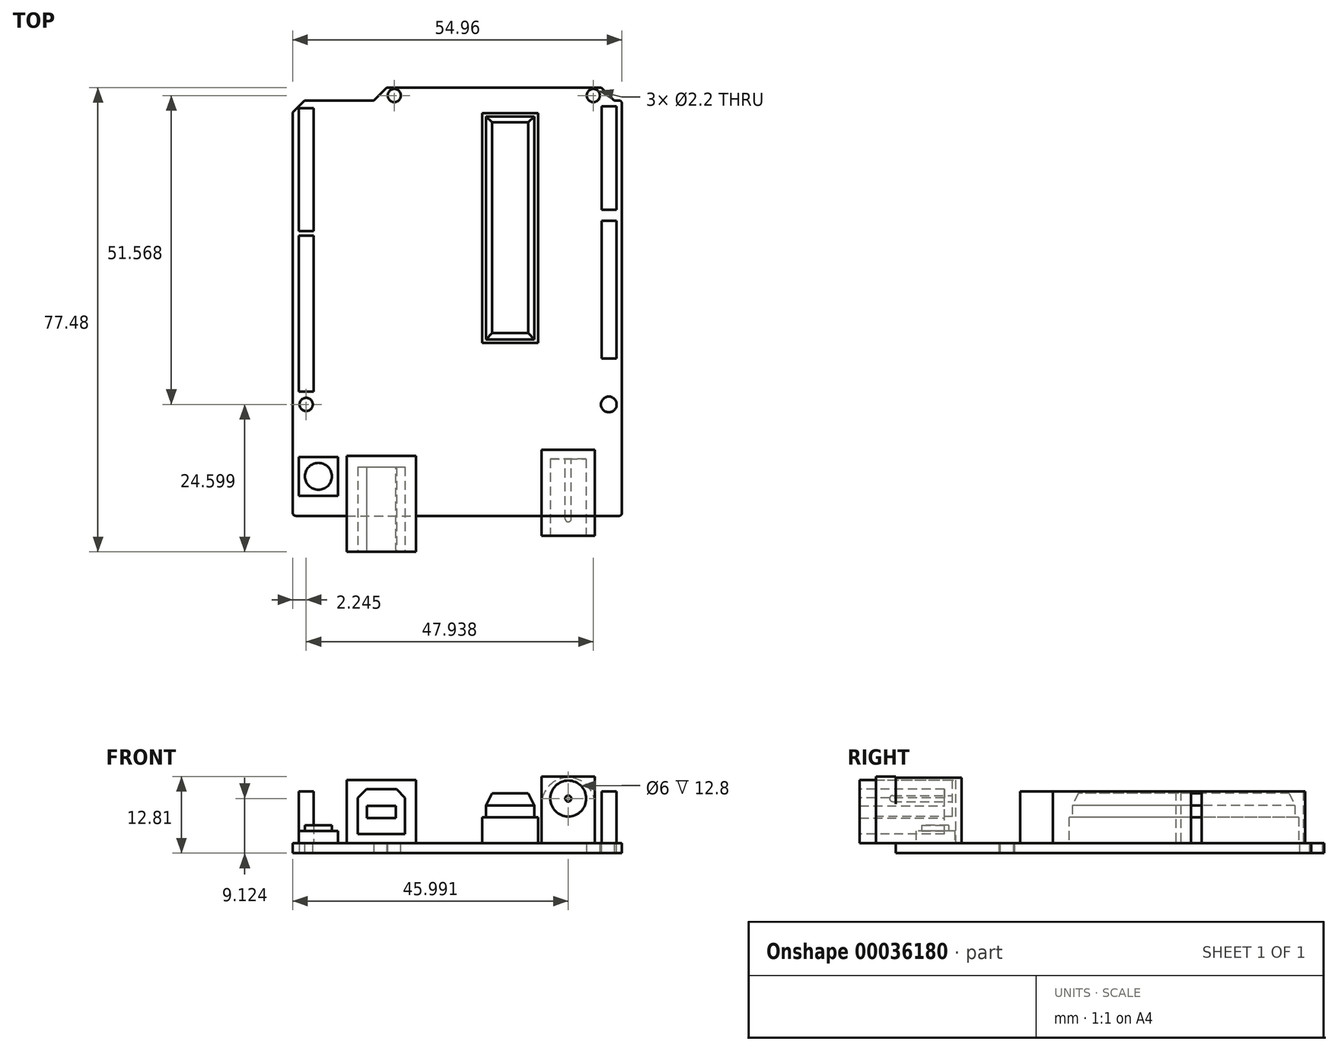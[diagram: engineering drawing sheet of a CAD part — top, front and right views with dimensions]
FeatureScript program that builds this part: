
annotation { "Feature Type Name" : "Feature", "Feature Type Description" : "" }
export const myFeature = defineFeature(function(context is Context, id is Id, definition is map)
    precondition{}
    {
        {
            var Q0;
            Q0=qCreatedBy(makeId("Top.planeOp"),FACE);
            var sketch = newSketch(context, id + "F0", { "sketchPlane" : qUnion([Q0])});
            skLineSegment(sketch, "E0.rect.bottom", {"start": v(-11.81, 35.74) * mm, "end": v(24.03, 35.74) * mm});
            skLineSegment(sketch, "E0.rect.top", {"start": v(-26.94, -35.74) * mm, "end": v(26.97, -35.74) * mm});
            skLineSegment(sketch, "E0.rect.left", {"start": v(-27.48, 31.62) * mm, "end": v(-27.48, -35.2) * mm});
            skLineSegment(sketch, "E0.rect.right", {"start": v(27.48, 33.07) * mm, "end": v(27.48, -35.23) * mm});
            skPoint(sketch, "E0.rect.middle", {"position": v(0, 0) * mm});
            skLineSegment(sketch, "E1.top", {"start": v(-25.49, 33.6) * mm, "end": v(-13.95, 33.6) * mm});
            skPoint(sketch, "E2.orphan", {"position": v(-27.48, 35.74) * mm});
            skLineSegment(sketch, "E3", {"start": v(-27.48, 31.62) * mm, "end": v(-25.49, 33.6) * mm});
            skLineSegment(sketch, "E4", {"start": v(-11.81, 35.74) * mm, "end": v(-13.95, 33.6) * mm});
            skLineSegment(sketch, "E5.top", {"start": v(26.17, 33.6) * mm, "end": v(26.94, 33.6) * mm});
            skLineSegment(sketch, "E6", {"start": v(24.03, 35.74) * mm, "end": v(26.17, 33.6) * mm});
            skPoint(sketch, "E7.orphan", {"position": v(27.48, 35.74) * mm});
            skPoint(sketch, "E8.visualSharp", {"position": v(27.48, -35.74) * mm});
            skArc(sketch, "E8.filletArc", {"start": v(26.97, -35.74) * mm, "mid": v(27.33, -35.6) * mm, "end": v(27.48, -35.23) * mm});
            skPoint(sketch, "E9.visualSharp", {"position": v(27.48, 33.6) * mm});
            skArc(sketch, "E9.filletArc", {"start": v(27.48, 33.07) * mm, "mid": v(27.32, 33.45) * mm, "end": v(26.94, 33.6) * mm});
            skPoint(sketch, "E10.visualSharp", {"position": v(-27.48, -35.74) * mm});
            skArc(sketch, "E10.filletArc", {"start": v(-27.48, -35.2) * mm, "mid": v(-27.32, -35.59) * mm, "end": v(-26.94, -35.74) * mm});
            skPoint(sketch, "E11.second.point", {"position": v(21.12, -10.57) * mm});
            skPoint(sketch, "E11.third.point", {"position": v(22.07, -8.93) * mm});
            skLineSegment(sketch, "E12", {"start": v(-13.95, 33.6) * mm, "end": v(31.22, 33.6) * mm, "construction": true});
            skSolve(sketch);
        }
        {
            var Q0;
            Q0=makeQuery(id+"F0.imprint","IMPRINT",FACE,{"disambiguationData":[TD([[makeQuery(id+"F0.imprint","IMPRINT",EDGE,{"derivedFrom":sQuery(id+"F0.wireOp",EDGE,"E0.rect.bottom")}),-1.0]])]});
            extrude(context, id + "F1", {"entities" : qUnion([Q0]), "depth" : 1.69 * mm});
        }
        {
            var Q0;
            Q0=makeQuery(id+"F1.opExtrude","CAP_FACE",FACE,{"disambiguationData":[OSD([sQuery(id+"F0.wireOp",EDGE,"E0.rect.bottom"),sQuery(id+"F0.wireOp",EDGE,"E0.rect.top"),sQuery(id+"F0.wireOp",EDGE,"E0.rect.left"),sQuery(id+"F0.wireOp",EDGE,"E0.rect.right"),sQuery(id+"F0.wireOp",EDGE,"E1.top"),sQuery(id+"F0.wireOp",EDGE,"E3"),sQuery(id+"F0.wireOp",EDGE,"E4"),sQuery(id+"F0.wireOp",EDGE,"E5.top"),sQuery(id+"F0.wireOp",EDGE,"E6"),sQuery(id+"F0.wireOp",EDGE,"E8.filletArc"),sQuery(id+"F0.wireOp",EDGE,"E9.filletArc"),sQuery(id+"F0.wireOp",EDGE,"E10.filletArc")])],"isStart":false});
            var sketch = newSketch(context, id + "F2", { "sketchPlane" : qUnion([Q0])});
            skLineSegment(sketch, "E13.top", {"start": v(24.1, -9.48) * mm, "end": v(26.53, -9.48) * mm});
            skLineSegment(sketch, "E13.left", {"start": v(24.1, 32.6) * mm, "end": v(24.1, 15.32) * mm});
            skLineSegment(sketch, "E13.right", {"start": v(26.53, 32.6) * mm, "end": v(26.53, 15.32) * mm});
            skLineSegment(sketch, "E14", {"start": v(24.1, 32.6) * mm, "end": v(26.53, 32.6) * mm});
            skLineSegment(sketch, "E15", {"start": v(24.1, 15.32) * mm, "end": v(26.53, 15.32) * mm});
            skLineSegment(sketch, "E16", {"start": v(24.1, 13.52) * mm, "end": v(26.53, 13.52) * mm});
            skLineSegment(sketch, "E17.trimOffspring", {"start": v(24.1, 13.52) * mm, "end": v(24.1, -9.48) * mm});
            skLineSegment(sketch, "E18.trimOffspring", {"start": v(26.53, 13.52) * mm, "end": v(26.53, -9.48) * mm});
            skLineSegment(sketch, "E19.bottom", {"start": v(-26.48, 32.3) * mm, "end": v(-23.98, 32.3) * mm});
            skLineSegment(sketch, "E19.top", {"start": v(-26.48, -14.99) * mm, "end": v(-23.98, -14.99) * mm});
            skLineSegment(sketch, "E19.left", {"start": v(-26.48, 32.3) * mm, "end": v(-26.48, 11.81) * mm});
            skLineSegment(sketch, "E19.right", {"start": v(-23.98, 32.3) * mm, "end": v(-23.98, 11.81) * mm});
            skLineSegment(sketch, "E20.bottom", {"start": v(-26.48, 11.81) * mm, "end": v(-23.98, 11.81) * mm});
            skLineSegment(sketch, "E20.top", {"start": v(-26.48, 11.01) * mm, "end": v(-23.98, 11.01) * mm});
            skLineSegment(sketch, "E21.trimOffspring", {"start": v(-23.98, 11.01) * mm, "end": v(-23.98, -14.99) * mm});
            skLineSegment(sketch, "E22.trimOffspring", {"start": v(-26.48, 11.01) * mm, "end": v(-26.48, -14.99) * mm});
            skSolve(sketch);
        }
        {
            var Q0;
            Q0=makeQuery(id+"F2.imprint","IMPRINT",FACE,{"disambiguationData":[TD([[makeQuery(id+"F2.imprint","IMPRINT",EDGE,{"derivedFrom":sQuery(id+"F2.wireOp",EDGE,"E13.top")}),1.0]])]});
            var Q1;
            Q1=makeQuery(id+"F2.imprint","IMPRINT",FACE,{"disambiguationData":[TD([[makeQuery(id+"F2.imprint","IMPRINT",EDGE,{"derivedFrom":sQuery(id+"F2.wireOp",EDGE,"E13.left")}),1.0]])]});
            var Q2;
            Q2=makeQuery(id+"F2.imprint","IMPRINT",FACE,{"disambiguationData":[TD([[makeQuery(id+"F2.imprint","IMPRINT",EDGE,{"derivedFrom":sQuery(id+"F2.wireOp",EDGE,"E19.bottom")}),-1.0]])]});
            var Q3;
            Q3=makeQuery(id+"F2.imprint","IMPRINT",FACE,{"disambiguationData":[TD([[makeQuery(id+"F2.imprint","IMPRINT",EDGE,{"derivedFrom":sQuery(id+"F2.wireOp",EDGE,"E19.top")}),1.0]])]});
            extrude(context, id + "F3", {"entities" : qUnion([Q0, Q1, Q2, Q3]), "depth" : 8.6 * mm});
        }
        {
            var Q0;
            Q0=makeQuery(id+"F1.opExtrude","SWEPT_FACE",FACE,{"disambiguationData":[OSD([sQuery(id+"F0.wireOp",EDGE,"E0.rect.top")])]});
            cPlane(context, id + "F4", {"entities" : qUnion([Q0]), "cplaneType" : CPlaneType.OFFSET, "offset" : 0 * mm, "width" : 150 * mm, "height" : 150 * mm});
        }
        {
            var Q0;
            Q0=qCreatedBy(id+"F4.planeOp",FACE);
            var sketch = newSketch(context, id + "F5", { "sketchPlane" : qUnion([Q0])});
            skLineSegment(sketch, "E23", {"start": v(30.92, 1.68) * mm, "end": v(22.95, 1.68) * mm, "construction": true});
            skLineSegment(sketch, "E24.bottom", {"start": v(22.95, 1.68) * mm, "end": v(14.07, 1.68) * mm});
            skLineSegment(sketch, "E24.left", {"start": v(22.95, 1.68) * mm, "end": v(22.95, 8.18) * mm});
            skLineSegment(sketch, "E24.right", {"start": v(14.07, 1.68) * mm, "end": v(14.07, 8.18) * mm});
            skArc(sketch, "E25", {"start": v(22.95, 8.18) * mm, "mid": v(18.51, 12.62) * mm, "end": v(14.07, 8.18) * mm});
            skSolve(sketch);
        }
        {
            var Q0;
            Q0=makeQuery(id+"F5.imprint","IMPRINT",FACE,{"disambiguationData":[TD([[makeQuery(id+"F5.imprint","IMPRINT",EDGE,{"derivedFrom":sQuery(id+"F5.wireOp",EDGE,"E24.bottom")}),-1.0]])]});
            extrude(context, id + "F6", {"entities" : qUnion([Q0]), "oppositeDirection" : true, "depth" : 11 * mm});
        }
        {
            var Q0;
            Q0=qCreatedBy(id+"F4.planeOp",FACE);
            var sketch = newSketch(context, id + "F7", { "sketchPlane" : qUnion([Q0])});
            skLineSegment(sketch, "E26.bottom", {"start": v(14.07, 1.69) * mm, "end": v(22.95, 1.69) * mm});
            skLineSegment(sketch, "E26.top", {"start": v(14.07, 12.81) * mm, "end": v(22.95, 12.81) * mm});
            skLineSegment(sketch, "E26.left", {"start": v(14.07, 1.69) * mm, "end": v(14.07, 12.81) * mm});
            skLineSegment(sketch, "E26.right", {"start": v(22.95, 1.69) * mm, "end": v(22.95, 12.81) * mm});
            skSolve(sketch);
        }
        {
            var Q0;
            Q0=makeQuery(id+"F7.imprint","IMPRINT",FACE,{"disambiguationData":[TD([[makeQuery(id+"F7.imprint","IMPRINT",EDGE,{"derivedFrom":sQuery(id+"F7.wireOp",EDGE,"E26.bottom")}),1.0]])]});
            extrude(context, id + "F8", {"entities" : qUnion([Q0]), "operationType" : NewBodyOperationType.ADD, "depth" : 3.3 * mm});
        }
        {
            var Q0;
            Q0=makeQuery(id+"F8.opExtrude","CAP_FACE",FACE,{"disambiguationData":[OSD([sQuery(id+"F7.wireOp",EDGE,"E26.bottom"),sQuery(id+"F7.wireOp",EDGE,"E26.top"),sQuery(id+"F7.wireOp",EDGE,"E26.left"),sQuery(id+"F7.wireOp",EDGE,"E26.right")])],"isStart":false});
            var sketch = newSketch(context, id + "F9", { "sketchPlane" : qUnion([Q0])});
            skCircle(sketch, "E27", {"center": v(18.51, 9.12) * mm, "radius": 3 * mm});
            skSolve(sketch);
        }
        {
            var Q0;
            Q0=makeQuery(id+"F9.imprint","IMPRINT",FACE,{"disambiguationData":[TD([[makeQuery(id+"F9.imprint","IMPRINT",EDGE,{"derivedFrom":sQuery(id+"F9.wireOp",EDGE,"E27")}),1.0]])]});
            var Q1;
            Q1=sQuery(id+"F9.wireOp",EDGE,"E27");
            extrude(context, id + "F10", {"entities" : qUnion([Q0]), "operationType" : NewBodyOperationType.REMOVE, "surfaceEntities" : qUnion([Q1]), "oppositeDirection" : true, "depth" : 12.8 * mm});
        }
        {
            var Q0;
            Q0=makeQuery(id+"F10.boolean.opBoolean","COPY",FACE,{"derivedFrom":makeQuery(id+"F10.opExtrude","CAP_FACE",FACE,{"disambiguationData":[OSD([sQuery(id+"F9.wireOp",EDGE,"E27")])],"isStart":false})});
            var sketch = newSketch(context, id + "F11", { "sketchPlane" : qUnion([Q0])});
            skCircle(sketch, "E28.0", {"center": v(18.51, 9.12) * mm, "radius": 3 * mm});
            skCircle(sketch, "E29", {"center": v(18.51, 9.12) * mm, "radius": 0.5 * mm});
            skSolve(sketch);
        }
        {
            var Q0;
            Q0=makeQuery(id+"F11.imprint","IMPRINT",FACE,{"disambiguationData":[TD([[makeQuery(id+"F11.imprint","IMPRINT",EDGE,{"derivedFrom":sQuery(id+"F11.wireOp",EDGE,"E29")}),1.0]])]});
            var Q1;
            Q1=sQuery(id+"F11.wireOp",EDGE,"E29");
            extrude(context, id + "F12", {"entities" : qUnion([Q0]), "surfaceEntities" : qUnion([Q1]), "depth" : 10 * mm});
        }
        {
            var Q0;
            Q0=makeQuery(id+"F1.opExtrude","CAP_FACE",FACE,{"disambiguationData":[OSD([sQuery(id+"F0.wireOp",EDGE,"E0.rect.bottom"),sQuery(id+"F0.wireOp",EDGE,"E0.rect.top"),sQuery(id+"F0.wireOp",EDGE,"E0.rect.left"),sQuery(id+"F0.wireOp",EDGE,"E0.rect.right"),sQuery(id+"F0.wireOp",EDGE,"E1.top"),sQuery(id+"F0.wireOp",EDGE,"E3"),sQuery(id+"F0.wireOp",EDGE,"E4"),sQuery(id+"F0.wireOp",EDGE,"E5.top"),sQuery(id+"F0.wireOp",EDGE,"E6"),sQuery(id+"F0.wireOp",EDGE,"E8.filletArc"),sQuery(id+"F0.wireOp",EDGE,"E9.filletArc"),sQuery(id+"F0.wireOp",EDGE,"E10.filletArc")])],"isStart":false});
            var sketch = newSketch(context, id + "F13", { "sketchPlane" : qUnion([Q0])});
            skLineSegment(sketch, "E30.bottom", {"start": v(-18.48, -35.74) * mm, "end": v(-6.88, -35.74) * mm});
            skLineSegment(sketch, "E30.top", {"start": v(-18.48, -25.74) * mm, "end": v(-6.88, -25.74) * mm});
            skLineSegment(sketch, "E30.left", {"start": v(-18.48, -35.74) * mm, "end": v(-18.48, -25.74) * mm});
            skLineSegment(sketch, "E30.right", {"start": v(-6.88, -35.74) * mm, "end": v(-6.88, -25.74) * mm});
            skSolve(sketch);
        }
        {
            var Q0;
            Q0=makeQuery(id+"F13.imprint","IMPRINT",FACE,{"disambiguationData":[TD([[makeQuery(id+"F13.imprint","IMPRINT",EDGE,{"derivedFrom":sQuery(id+"F13.wireOp",EDGE,"E30.bottom")}),1.0]])]});
            extrude(context, id + "F14", {"entities" : qUnion([Q0]), "depth" : 10.5 * mm});
        }
        {
            var Q0;
            Q0=makeQuery(id+"F14.opExtrude","SWEPT_FACE",FACE,{"disambiguationData":[OSD([sQuery(id+"F13.wireOp",EDGE,"E30.bottom")])]});
            var sketch = newSketch(context, id + "F15", { "sketchPlane" : qUnion([Q0])});
            skLineSegment(sketch, "E31.bottom", {"start": v(-18.48, 12.2) * mm, "end": v(-6.88, 12.2) * mm});
            skLineSegment(sketch, "E31.top", {"start": v(-18.48, 1.69) * mm, "end": v(-6.88, 1.69) * mm});
            skLineSegment(sketch, "E31.left", {"start": v(-18.48, 12.2) * mm, "end": v(-18.48, 1.69) * mm});
            skLineSegment(sketch, "E31.right", {"start": v(-6.88, 12.2) * mm, "end": v(-6.88, 1.69) * mm});
            skSolve(sketch);
        }
        {
            var Q0;
            Q0=makeQuery(id+"F15.imprint","IMPRINT",FACE,{"disambiguationData":[TD([[makeQuery(id+"F15.imprint","IMPRINT",EDGE,{"derivedFrom":sQuery(id+"F15.wireOp",EDGE,"E31.bottom")}),-1.0]])]});
            extrude(context, id + "F16", {"entities" : qUnion([Q0]), "operationType" : NewBodyOperationType.ADD, "depth" : 6 * mm});
        }
        {
            var Q0;
            Q0=makeQuery(id+"F16.opExtrude","CAP_FACE",FACE,{"disambiguationData":[OSD([sQuery(id+"F15.wireOp",EDGE,"E31.bottom"),sQuery(id+"F15.wireOp",EDGE,"E31.top"),sQuery(id+"F15.wireOp",EDGE,"E31.left"),sQuery(id+"F15.wireOp",EDGE,"E31.right")])],"isStart":false});
            var sketch = newSketch(context, id + "F17", { "sketchPlane" : qUnion([Q0])});
            skLineSegment(sketch, "E32.rect.bottom", {"start": v(-16.63, 3.2) * mm, "end": v(-8.73, 3.2) * mm});
            skLineSegment(sketch, "E32.rect.top", {"start": v(-15.19, 10.7) * mm, "end": v(-10.17, 10.7) * mm});
            skLineSegment(sketch, "E32.rect.left", {"start": v(-16.63, 3.2) * mm, "end": v(-16.63, 9.25) * mm});
            skLineSegment(sketch, "E32.rect.right", {"start": v(-8.73, 3.2) * mm, "end": v(-8.73, 9.25) * mm});
            skPoint(sketch, "E32.rect.middle", {"position": v(-12.68, 6.94) * mm});
            skPoint(sketch, "E32.rect.middle.positionSnap0", {"position": v(-18.48, 6.94) * mm});
            skPoint(sketch, "E32.rect.middle.positionSnap1", {"position": v(-12.68, 12.2) * mm});
            skPoint(sketch, "E32.rect.centerSnap0", {"position": v(-18.48, 6.94) * mm});
            skPoint(sketch, "E32.rect.centerSnap1", {"position": v(-12.68, 12.2) * mm});
            skLineSegment(sketch, "E33", {"start": v(-16.63, 9.25) * mm, "end": v(-15.19, 10.7) * mm});
            skLineSegment(sketch, "E34", {"start": v(-10.17, 10.7) * mm, "end": v(-8.73, 9.25) * mm});
            skPoint(sketch, "E35.orphan", {"position": v(-16.63, 10.7) * mm});
            skPoint(sketch, "E36.orphan", {"position": v(-8.73, 10.7) * mm});
            skSolve(sketch);
        }
        {
            var Q0;
            Q0=makeQuery(id+"F17.imprint","IMPRINT",FACE,{"disambiguationData":[TD([[makeQuery(id+"F17.imprint","IMPRINT",EDGE,{"derivedFrom":sQuery(id+"F17.wireOp",EDGE,"E32.rect.bottom")}),1.0]])]});
            extrude(context, id + "F18", {"entities" : qUnion([Q0]), "operationType" : NewBodyOperationType.REMOVE, "oppositeDirection" : true, "depth" : 14.14 * mm});
        }
        {
            var Q0;
            Q0=makeQuery(id+"F18.boolean.opBoolean","COPY",FACE,{"derivedFrom":makeQuery(id+"F18.opExtrude","CAP_FACE",FACE,{"disambiguationData":[OSD([sQuery(id+"F17.wireOp",EDGE,"E32.rect.bottom"),sQuery(id+"F17.wireOp",EDGE,"E32.rect.top"),sQuery(id+"F17.wireOp",EDGE,"E32.rect.left"),sQuery(id+"F17.wireOp",EDGE,"E32.rect.right"),sQuery(id+"F17.wireOp",EDGE,"E33"),sQuery(id+"F17.wireOp",EDGE,"E34")])],"isStart":false})});
            var sketch = newSketch(context, id + "F19", { "sketchPlane" : qUnion([Q0])});
            skLineSegment(sketch, "E37.rect.bottom", {"start": v(-15.12, 5.84) * mm, "end": v(-10.24, 5.84) * mm});
            skLineSegment(sketch, "E37.rect.top", {"start": v(-15.12, 7.92) * mm, "end": v(-10.24, 7.92) * mm});
            skLineSegment(sketch, "E37.rect.left", {"start": v(-15.12, 5.84) * mm, "end": v(-15.12, 7.92) * mm});
            skLineSegment(sketch, "E37.rect.right", {"start": v(-10.24, 5.84) * mm, "end": v(-10.24, 7.92) * mm});
            skPoint(sketch, "E37.rect.middle", {"position": v(-12.68, 6.88) * mm});
            skPoint(sketch, "E37.rect.middle.positionSnap0", {"position": v(-12.68, 10.7) * mm});
            skPoint(sketch, "E37.rect.centerSnap0", {"position": v(-12.68, 10.7) * mm});
            skSolve(sketch);
        }
        {
            var Q0;
            Q0 = qSketchRegion(id + "F19", true);
            var Q1;
            Q1=makeQuery(id+"F16.opExtrude","CAP_FACE",FACE,{"disambiguationData":[OSD([sQuery(id+"F15.wireOp",EDGE,"E31.bottom"),sQuery(id+"F15.wireOp",EDGE,"E31.top"),sQuery(id+"F15.wireOp",EDGE,"E31.left"),sQuery(id+"F15.wireOp",EDGE,"E31.right")])],"isStart":false});
            extrude(context, id + "F20", {"entities" : qUnion([Q0]), "endBound" : BoundingType.UP_TO_SURFACE, "endBoundEntityFace" : qUnion([Q1]), "depth" : 25 * mm});
        }
        {
            var Q0;
            Q0=makeQuery(id+"F1.opExtrude","CAP_FACE",FACE,{"disambiguationData":[OSD([sQuery(id+"F0.wireOp",EDGE,"E0.rect.bottom"),sQuery(id+"F0.wireOp",EDGE,"E0.rect.top"),sQuery(id+"F0.wireOp",EDGE,"E0.rect.left"),sQuery(id+"F0.wireOp",EDGE,"E0.rect.right"),sQuery(id+"F0.wireOp",EDGE,"E1.top"),sQuery(id+"F0.wireOp",EDGE,"E3"),sQuery(id+"F0.wireOp",EDGE,"E4"),sQuery(id+"F0.wireOp",EDGE,"E5.top"),sQuery(id+"F0.wireOp",EDGE,"E6"),sQuery(id+"F0.wireOp",EDGE,"E8.filletArc"),sQuery(id+"F0.wireOp",EDGE,"E9.filletArc"),sQuery(id+"F0.wireOp",EDGE,"E10.filletArc")])],"isStart":false});
            var sketch = newSketch(context, id + "F21", { "sketchPlane" : qUnion([Q0])});
            skLineSegment(sketch, "E38.rect.bottom", {"start": v(-26.44, -25.9) * mm, "end": v(-19.94, -25.9) * mm});
            skLineSegment(sketch, "E38.rect.top", {"start": v(-26.44, -32.4) * mm, "end": v(-19.94, -32.4) * mm});
            skLineSegment(sketch, "E38.rect.left", {"start": v(-26.44, -25.9) * mm, "end": v(-26.44, -32.4) * mm});
            skLineSegment(sketch, "E38.rect.right", {"start": v(-19.94, -25.9) * mm, "end": v(-19.94, -32.4) * mm});
            skPoint(sketch, "E38.rect.middle", {"position": v(-23.19, -29.14) * mm});
            skSolve(sketch);
        }
        {
            var Q0;
            Q0=makeQuery(id+"F21.imprint","IMPRINT",FACE,{"disambiguationData":[TD([[makeQuery(id+"F21.imprint","IMPRINT",EDGE,{"derivedFrom":sQuery(id+"F21.wireOp",EDGE,"E38.rect.bottom")}),-1.0]])]});
            extrude(context, id + "F22", {"entities" : qUnion([Q0]), "depth" : 2 * mm});
        }
        {
            var Q0;
            Q0=makeQuery(id+"F22.opExtrude","CAP_FACE",FACE,{"disambiguationData":[OSD([sQuery(id+"F21.wireOp",EDGE,"E38.rect.bottom"),sQuery(id+"F21.wireOp",EDGE,"E38.rect.top"),sQuery(id+"F21.wireOp",EDGE,"E38.rect.left"),sQuery(id+"F21.wireOp",EDGE,"E38.rect.right")])],"isStart":false});
            var sketch = newSketch(context, id + "F23", { "sketchPlane" : qUnion([Q0])});
            skCircle(sketch, "E39", {"center": v(-23.19, -29.14) * mm, "radius": 2.24 * mm});
            skPoint(sketch, "E39.centerSnap0", {"position": v(-26.44, -29.14) * mm});
            skSolve(sketch);
        }
        {
            var Q0;
            Q0=makeQuery(id+"F23.imprint","IMPRINT",FACE,{"disambiguationData":[TD([[makeQuery(id+"F23.imprint","IMPRINT",EDGE,{"derivedFrom":sQuery(id+"F23.wireOp",EDGE,"E39")}),1.0]])]});
            extrude(context, id + "F24", {"entities" : qUnion([Q0]), "depth" : 1 * mm});
        }
        {
            var Q0;
            Q0=makeQuery(id+"F1.opExtrude","CAP_FACE",FACE,{"disambiguationData":[OSD([sQuery(id+"F0.wireOp",EDGE,"E0.rect.bottom"),sQuery(id+"F0.wireOp",EDGE,"E0.rect.top"),sQuery(id+"F0.wireOp",EDGE,"E0.rect.left"),sQuery(id+"F0.wireOp",EDGE,"E0.rect.right"),sQuery(id+"F0.wireOp",EDGE,"E1.top"),sQuery(id+"F0.wireOp",EDGE,"E3"),sQuery(id+"F0.wireOp",EDGE,"E4"),sQuery(id+"F0.wireOp",EDGE,"E5.top"),sQuery(id+"F0.wireOp",EDGE,"E6"),sQuery(id+"F0.wireOp",EDGE,"E8.filletArc"),sQuery(id+"F0.wireOp",EDGE,"E9.filletArc"),sQuery(id+"F0.wireOp",EDGE,"E10.filletArc")])],"isStart":false});
            var sketch = newSketch(context, id + "F25", { "sketchPlane" : qUnion([Q0])});
            skLineSegment(sketch, "E40.bottom", {"start": v(13.47, 31.5) * mm, "end": v(4.14, 31.5) * mm});
            skLineSegment(sketch, "E40.top", {"start": v(13.47, -6.87) * mm, "end": v(4.14, -6.87) * mm});
            skLineSegment(sketch, "E40.left", {"start": v(13.47, 31.5) * mm, "end": v(13.47, -6.87) * mm});
            skLineSegment(sketch, "E40.right", {"start": v(4.14, 31.5) * mm, "end": v(4.14, -6.87) * mm});
            skSolve(sketch);
        }
        {
            var Q0;
            Q0=makeQuery(id+"F25.imprint","IMPRINT",FACE,{"disambiguationData":[TD([[makeQuery(id+"F25.imprint","IMPRINT",EDGE,{"derivedFrom":sQuery(id+"F25.wireOp",EDGE,"E40.bottom")}),1.0]])]});
            extrude(context, id + "F26", {"entities" : qUnion([Q0]), "depth" : 4.3 * mm});
        }
        {
            var Q0;
            Q0=makeQuery(id+"F26.opExtrude","CAP_FACE",FACE,{"disambiguationData":[OSD([sQuery(id+"F25.wireOp",EDGE,"E40.bottom"),sQuery(id+"F25.wireOp",EDGE,"E40.top"),sQuery(id+"F25.wireOp",EDGE,"E40.left"),sQuery(id+"F25.wireOp",EDGE,"E40.right")])],"isStart":false});
            var sketch = newSketch(context, id + "F27", { "sketchPlane" : qUnion([Q0])});
            skLineSegment(sketch, "E41.rect.bottom", {"start": v(4.76, 30.91) * mm, "end": v(12.84, 30.91) * mm});
            skLineSegment(sketch, "E41.rect.top", {"start": v(4.76, -6.28) * mm, "end": v(12.84, -6.28) * mm});
            skLineSegment(sketch, "E41.rect.left", {"start": v(4.76, 30.91) * mm, "end": v(4.76, -6.28) * mm});
            skLineSegment(sketch, "E41.rect.right", {"start": v(12.84, 30.91) * mm, "end": v(12.84, -6.28) * mm});
            skPoint(sketch, "E41.rect.middle", {"position": v(8.8, 12.32) * mm});
            skPoint(sketch, "E41.rect.middle.positionSnap0", {"position": v(8.8, 31.5) * mm});
            skPoint(sketch, "E41.rect.middle.positionSnap1", {"position": v(4.14, 12.32) * mm});
            skPoint(sketch, "E41.rect.centerSnap0", {"position": v(8.8, 31.5) * mm});
            skPoint(sketch, "E41.rect.centerSnap1", {"position": v(4.14, 12.32) * mm});
            skSolve(sketch);
        }
        {
            var Q0;
            Q0=makeQuery(id+"F27.imprint","IMPRINT",FACE,{"disambiguationData":[TD([[makeQuery(id+"F27.imprint","IMPRINT",EDGE,{"derivedFrom":sQuery(id+"F27.wireOp",EDGE,"E41.rect.bottom")}),-1.0]])]});
            extrude(context, id + "F28", {"entities" : qUnion([Q0]), "depth" : 2 * mm});
        }
        {
            var Q0;
            Q0=makeQuery(id+"F28.opExtrude","CAP_FACE",FACE,{"disambiguationData":[OSD([sQuery(id+"F27.wireOp",EDGE,"E41.rect.bottom"),sQuery(id+"F27.wireOp",EDGE,"E41.rect.top"),sQuery(id+"F27.wireOp",EDGE,"E41.rect.left"),sQuery(id+"F27.wireOp",EDGE,"E41.rect.right")])],"isStart":false});
            cPlane(context, id + "F29", {"entities" : qUnion([Q0]), "cplaneType" : CPlaneType.OFFSET, "offset" : 2 * mm, "width" : 150 * mm, "height" : 150 * mm});
        }
        {
            var Q0;
            Q0=qCreatedBy(id+"F29.planeOp",FACE);
            var sketch = newSketch(context, id + "F30", { "sketchPlane" : qUnion([Q0])});
            skLineSegment(sketch, "E42.bottom", {"start": v(5.78, 29.94) * mm, "end": v(11.83, 29.94) * mm});
            skLineSegment(sketch, "E42.top", {"start": v(5.78, -5.22) * mm, "end": v(11.83, -5.22) * mm});
            skLineSegment(sketch, "E42.left", {"start": v(5.78, 29.94) * mm, "end": v(5.78, -5.22) * mm});
            skLineSegment(sketch, "E42.right", {"start": v(11.83, 29.94) * mm, "end": v(11.83, -5.22) * mm});
            skSolve(sketch);
        }
        {
            var Q1;
            Q1=makeQuery(id+"F30.imprint","IMPRINT",FACE,{"disambiguationData":[TD([[makeQuery(id+"F30.imprint","IMPRINT",EDGE,{"derivedFrom":sQuery(id+"F30.wireOp",EDGE,"E42.bottom")}),-1.0]])]});
            var Q2;
            Q2=makeQuery(id+"F28.opExtrude","CAP_FACE",FACE,{"disambiguationData":[OSD([sQuery(id+"F27.wireOp",EDGE,"E41.rect.bottom"),sQuery(id+"F27.wireOp",EDGE,"E41.rect.top"),sQuery(id+"F27.wireOp",EDGE,"E41.rect.left"),sQuery(id+"F27.wireOp",EDGE,"E41.rect.right")])],"isStart":false});
            loft(context, id + "F31", {"sheetProfilesArray" : [{ "sheetProfileEntities" : qUnion([Q1]) }, { "sheetProfileEntities" : qUnion([Q2]) }]});
        }
        {
            var Q0;
            Q0=makeQuery(id+"F1.opExtrude","CAP_FACE",FACE,{"disambiguationData":[OSD([sQuery(id+"F0.wireOp",EDGE,"E0.rect.bottom"),sQuery(id+"F0.wireOp",EDGE,"E0.rect.top"),sQuery(id+"F0.wireOp",EDGE,"E0.rect.left"),sQuery(id+"F0.wireOp",EDGE,"E0.rect.right"),sQuery(id+"F0.wireOp",EDGE,"E1.top"),sQuery(id+"F0.wireOp",EDGE,"E3"),sQuery(id+"F0.wireOp",EDGE,"E4"),sQuery(id+"F0.wireOp",EDGE,"E5.top"),sQuery(id+"F0.wireOp",EDGE,"E6"),sQuery(id+"F0.wireOp",EDGE,"E8.filletArc"),sQuery(id+"F0.wireOp",EDGE,"E9.filletArc"),sQuery(id+"F0.wireOp",EDGE,"E10.filletArc")])],"isStart":false});
            var sketch = newSketch(context, id + "F32", { "sketchPlane" : qUnion([Q0])});
            skCircle(sketch, "E43", {"center": v(-10.52, 34.43) * mm, "radius": 1.1 * mm});
            skCircle(sketch, "E44", {"center": v(22.7, 34.43) * mm, "radius": 1.1 * mm});
            skSolve(sketch);
        }
        {
            var Q0;
            Q0=makeQuery(id+"F32.imprint","IMPRINT",FACE,{"disambiguationData":[TD([[makeQuery(id+"F32.imprint","IMPRINT",EDGE,{"derivedFrom":sQuery(id+"F32.wireOp",EDGE,"E43")}),1.0]])]});
            var Q1;
            Q1=makeQuery(id+"F32.imprint","IMPRINT",FACE,{"disambiguationData":[TD([[makeQuery(id+"F32.imprint","IMPRINT",EDGE,{"derivedFrom":sQuery(id+"F32.wireOp",EDGE,"E44")}),1.0]])]});
            extrude(context, id + "F33", {"entities" : qUnion([Q0, Q1]), "operationType" : NewBodyOperationType.REMOVE, "endBound" : BoundingType.THROUGH_ALL, "oppositeDirection" : true, "depth" : 25 * mm});
        }
        {
            var Q0;
            Q0=makeQuery(id+"F1.opExtrude","CAP_FACE",FACE,{"disambiguationData":[OSD([sQuery(id+"F0.wireOp",EDGE,"E0.rect.bottom"),sQuery(id+"F0.wireOp",EDGE,"E0.rect.top"),sQuery(id+"F0.wireOp",EDGE,"E0.rect.left"),sQuery(id+"F0.wireOp",EDGE,"E0.rect.right"),sQuery(id+"F0.wireOp",EDGE,"E1.top"),sQuery(id+"F0.wireOp",EDGE,"E3"),sQuery(id+"F0.wireOp",EDGE,"E4"),sQuery(id+"F0.wireOp",EDGE,"E5.top"),sQuery(id+"F0.wireOp",EDGE,"E6"),sQuery(id+"F0.wireOp",EDGE,"E8.filletArc"),sQuery(id+"F0.wireOp",EDGE,"E9.filletArc"),sQuery(id+"F0.wireOp",EDGE,"E10.filletArc")])],"isStart":false});
            var sketch = newSketch(context, id + "F34", { "sketchPlane" : qUnion([Q0])});
            skCircle(sketch, "E45", {"center": v(-25.23, -17.14) * mm, "radius": 1.1 * mm});
            skCircle(sketch, "E46", {"center": v(25.28, -17.14) * mm, "radius": 1.31 * mm});
            skSolve(sketch);
        }
        {
            var Q0;
            Q0=makeQuery(id+"F34.imprint","IMPRINT",FACE,{"disambiguationData":[TD([[makeQuery(id+"F34.imprint","IMPRINT",EDGE,{"derivedFrom":sQuery(id+"F34.wireOp",EDGE,"E45")}),1.0]])]});
            var Q1;
            Q1=makeQuery(id+"F34.imprint","IMPRINT",FACE,{"disambiguationData":[TD([[makeQuery(id+"F34.imprint","IMPRINT",EDGE,{"derivedFrom":sQuery(id+"F34.wireOp",EDGE,"E46")}),1.0]])]});
            var Q2;
            Q2=sQuery(id+"F34.wireOp",EDGE,"E45");
            var Q3;
            Q3=sQuery(id+"F34.wireOp",EDGE,"E46");
            extrude(context, id + "F35", {"entities" : qUnion([Q0, Q1]), "operationType" : NewBodyOperationType.REMOVE, "surfaceEntities" : qUnion([Q2, Q3]), "endBound" : BoundingType.THROUGH_ALL, "oppositeDirection" : true, "depth" : 25 * mm});
        }
        {
            var Q0;
            Q0=makeQuery(id+"F12.opExtrude","CAP_FACE",FACE,{"disambiguationData":[OSD([sQuery(id+"F11.wireOp",EDGE,"E29")])],"isStart":false});
            var sketch = newSketch(context, id + "F36", { "sketchPlane" : qUnion([Q0])});
            skArc(sketch, "E47.0", {"start": v(18.51, 9.62) * mm, "mid": v(18.01, 9.12) * mm, "end": v(18.51, 8.62) * mm});
            skLineSegment(sketch, "E48", {"start": v(18.51, 9.62) * mm, "end": v(18.51, 8.62) * mm});
            skSolve(sketch);
        }
        {
            var Q0;
            {var subQ2=sQuery(id+"F36.wireOp",EDGE,"E48");Q0=makeQuery(id+"F36.imprint","IMPRINT",FACE,{"disambiguationData":[TD([[makeQuery(id+"F36.imprint","IMPRINT",EDGE,{"derivedFrom":subQ2}),1.0]])]});}
            var Q1;
            Q1=sQuery(id+"F36.wireOp",EDGE,"E48");
            revolve(context, id + "F37", {"operationType" : NewBodyOperationType.ADD, "entities" : qUnion([Q0]), "axis" : qUnion([Q1]), "revolveType" : RevolveType.ONE_DIRECTION, "angle" : 180 * degree});
        }
    });
